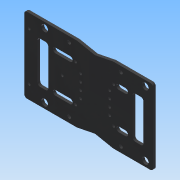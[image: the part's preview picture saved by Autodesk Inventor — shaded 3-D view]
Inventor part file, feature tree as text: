
AUTODESK INVENTOR PART (.ipt)
format: ipt  version: 2015 (Build 190159000, 159)  size: 566,272 bytes
history: native  units: mm
features: extrude x7, sketch x6, projected_geometry x4, fillet x3
ambient origin geometry x8: Origin, YZ Plane, XZ Plane, XY Plane, X Axis, Y Axis, Z Axis, Center Point
bodies: Solide1 (feature_tree)
feature tree (20):
  extrude  "Extrusion1"  Depth=40.0mm
  extrude  "Extrusion3"  Depth=8.0mm
  extrude  "Extrusion4"  Depth=27.0mm
  extrude  "Extrusion5"  Depth=71.0mm
  extrude  "Extrusion6"  Depth=111.0mm
  fillet  "Congé1"  [1 undecoded]
  fillet  "Congé2"  Radius=2.0mm
  extrude  "Extrusion7"  Depth=2.0mm
  fillet  "Congé3"  Radius=4.0mm
  extrude  "Extrusion8"  Depth=32.0mm
  sketch  "Esquisse4"
  projected_geometry  "Boucle projetée1"
  sketch  "Esquisse5"
  projected_geometry  "Boucle projetée2"
  sketch  "Esquisse6"
  sketch  "Esquisse7"
  projected_geometry  "Boucle projetée3"
  sketch  "Esquisse8"
  sketch  "Esquisse9"
  projected_geometry  "Boucle projetée4"
note: 1 required parameter value undecoded (feature->parameter linkage not recoverable at this tier; creation-order binding heuristic only, values carry confidence <= 0.55)
